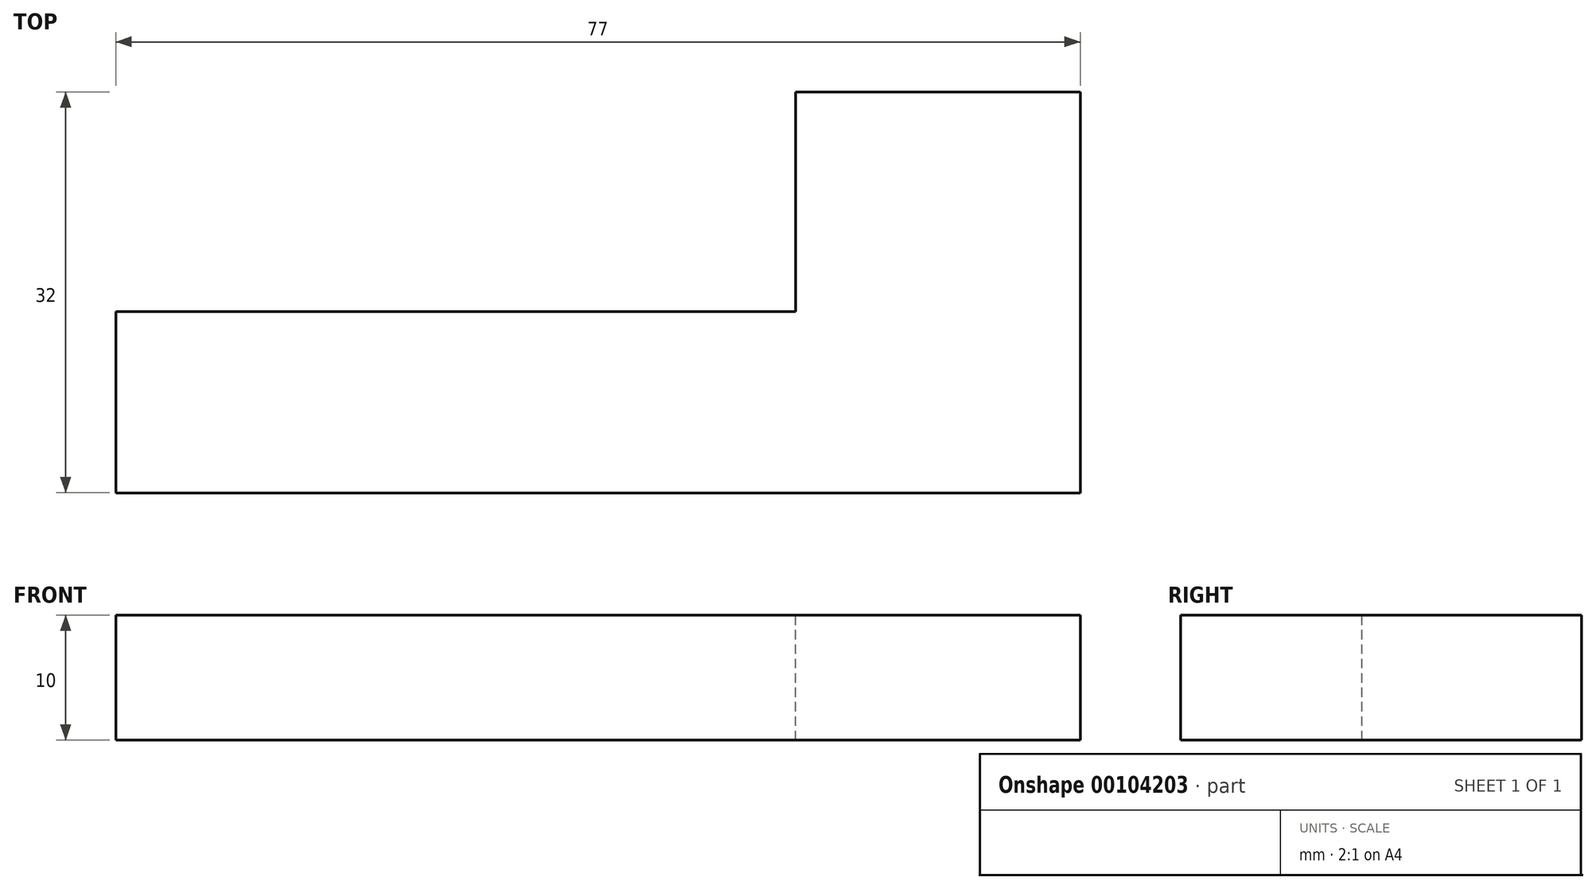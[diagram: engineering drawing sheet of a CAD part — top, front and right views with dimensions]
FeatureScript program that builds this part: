
annotation { "Feature Type Name" : "Feature", "Feature Type Description" : "" }
export const myFeature = defineFeature(function(context is Context, id is Id, definition is map)
    precondition{}
    {
        {
            var Q0;
            Q0=qCreatedBy(makeId("Top.planeOp"),FACE);
            var sketch = newSketch(context, id + "F0", { "sketchPlane" : qUnion([Q0])});
            skLineSegment(sketch, "E0.bottom", {"start": v(-48.26, 11.8) * mm, "end": v(28.74, 11.8) * mm});
            skLineSegment(sketch, "E0.top", {"start": v(-48.26, -20.2) * mm, "end": v(28.74, -20.2) * mm});
            skLineSegment(sketch, "E0.left", {"start": v(-48.26, 11.8) * mm, "end": v(-48.26, -20.2) * mm});
            skLineSegment(sketch, "E0.right", {"start": v(28.74, 11.8) * mm, "end": v(28.74, -20.2) * mm});
            skSolve(sketch);
        }
        {
            var Q0;
            Q0=makeQuery(id+"F0.imprint","IMPRINT",FACE,{"disambiguationData":[TD([[makeQuery(id+"F0.imprint","IMPRINT",EDGE,{"derivedFrom":sQuery(id+"F0.wireOp",EDGE,"E0.bottom")}),-1.0]])]});
            extrude(context, id + "F1", {"entities" : qUnion([Q0]), "depth" : 10 * mm});
        }
        {
            var Q0;
            Q0=makeQuery(id+"F1.opExtrude","CAP_FACE",FACE,{"disambiguationData":[OSD([sQuery(id+"F0.wireOp",EDGE,"E0.bottom"),sQuery(id+"F0.wireOp",EDGE,"E0.top"),sQuery(id+"F0.wireOp",EDGE,"E0.left"),sQuery(id+"F0.wireOp",EDGE,"E0.right")])],"isStart":false});
            var sketch = newSketch(context, id + "F2", { "sketchPlane" : qUnion([Q0])});
            skLineSegment(sketch, "E1.bottom", {"start": v(-48.26, 11.8) * mm, "end": v(6, 11.8) * mm});
            skLineSegment(sketch, "E1.top", {"start": v(-48.26, -5.73) * mm, "end": v(6, -5.73) * mm});
            skLineSegment(sketch, "E1.left", {"start": v(-48.26, 11.8) * mm, "end": v(-48.26, -5.73) * mm});
            skLineSegment(sketch, "E1.right", {"start": v(6, 11.8) * mm, "end": v(6, -5.73) * mm});
            skSolve(sketch);
        }
        {
            var Q0;
            Q0 = qSketchRegion(id + "F2", true);
            var Q1;
            Q1=makeQuery(id+"F2.imprint","IMPRINT",FACE,{"disambiguationData":[TD([[makeQuery(id+"F2.imprint","IMPRINT",EDGE,{"derivedFrom":sQuery(id+"F2.wireOp",EDGE,"E1.bottom")}),-1.0]])]});
            extrude(context, id + "F3", {"entities" : qUnion([Q0, Q1]), "operationType" : NewBodyOperationType.REMOVE, "endBound" : BoundingType.THROUGH_ALL, "oppositeDirection" : true, "depth" : 25 * mm});
        }
    });
